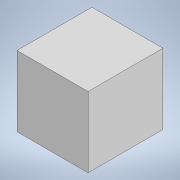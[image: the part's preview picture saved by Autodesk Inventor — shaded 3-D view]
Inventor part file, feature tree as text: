
AUTODESK INVENTOR PART (.ipt)
format: ipt  version: 2020 (Build 240168000, 168)  size: 84,480 bytes
history: native  units: mm
features: extrude x1, sketch x1
ambient origin geometry x8: Origin, YZ Plane, XZ Plane, XY Plane, X Axis, Y Axis, Z Axis, Center Point
bodies: Solid1 (feature_tree)
feature tree (2):
  extrude  "Extrusion1"  Depth=18.15mm
  sketch  "Sketch1"  dims[d0=18.3mm d1=18.15mm d2=19.3mm d3=0.0mm]
